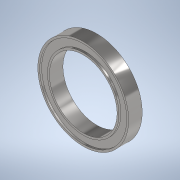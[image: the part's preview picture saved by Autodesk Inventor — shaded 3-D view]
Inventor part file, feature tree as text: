
AUTODESK INVENTOR PART (.ipt)
format: ipt  version: 2022 (Build 260153000, 153)  size: 138,752 bytes
history: native  units: in
note: dims shown in document units (in); Inventor stores cm internally (conversion verified against a paired STEP export)
features: extrude x3, sketch x3, projected_geometry x2
ambient origin geometry x8: Origin, YZ Plane, XZ Plane, XY Plane, X Axis, Y Axis, Z Axis, Center Point
bodies: Solid1 (feature_tree)
feature tree (8):
  extrude  "Extrusion1"  Depth=1.8504in
  extrude  "Extrusion2"  Depth=0.0394in
  extrude  "Extrusion3"  Depth=0.0394in TaperAngle=0.0deg
  sketch  "Sketch1"  dims[d0=1.378in d1=1.8504in]
  sketch  "Sketch2"  dims[d2=0.2756in d3=0.0in d4=0.0394in]
  projected_geometry  "Projected Loop1"
  sketch  "Sketch3"  dims[d5=0.0394in d6=0.0394in d7=0.0in d8=0.0394in d9=0.0in]
  projected_geometry  "Projected Loop2"
